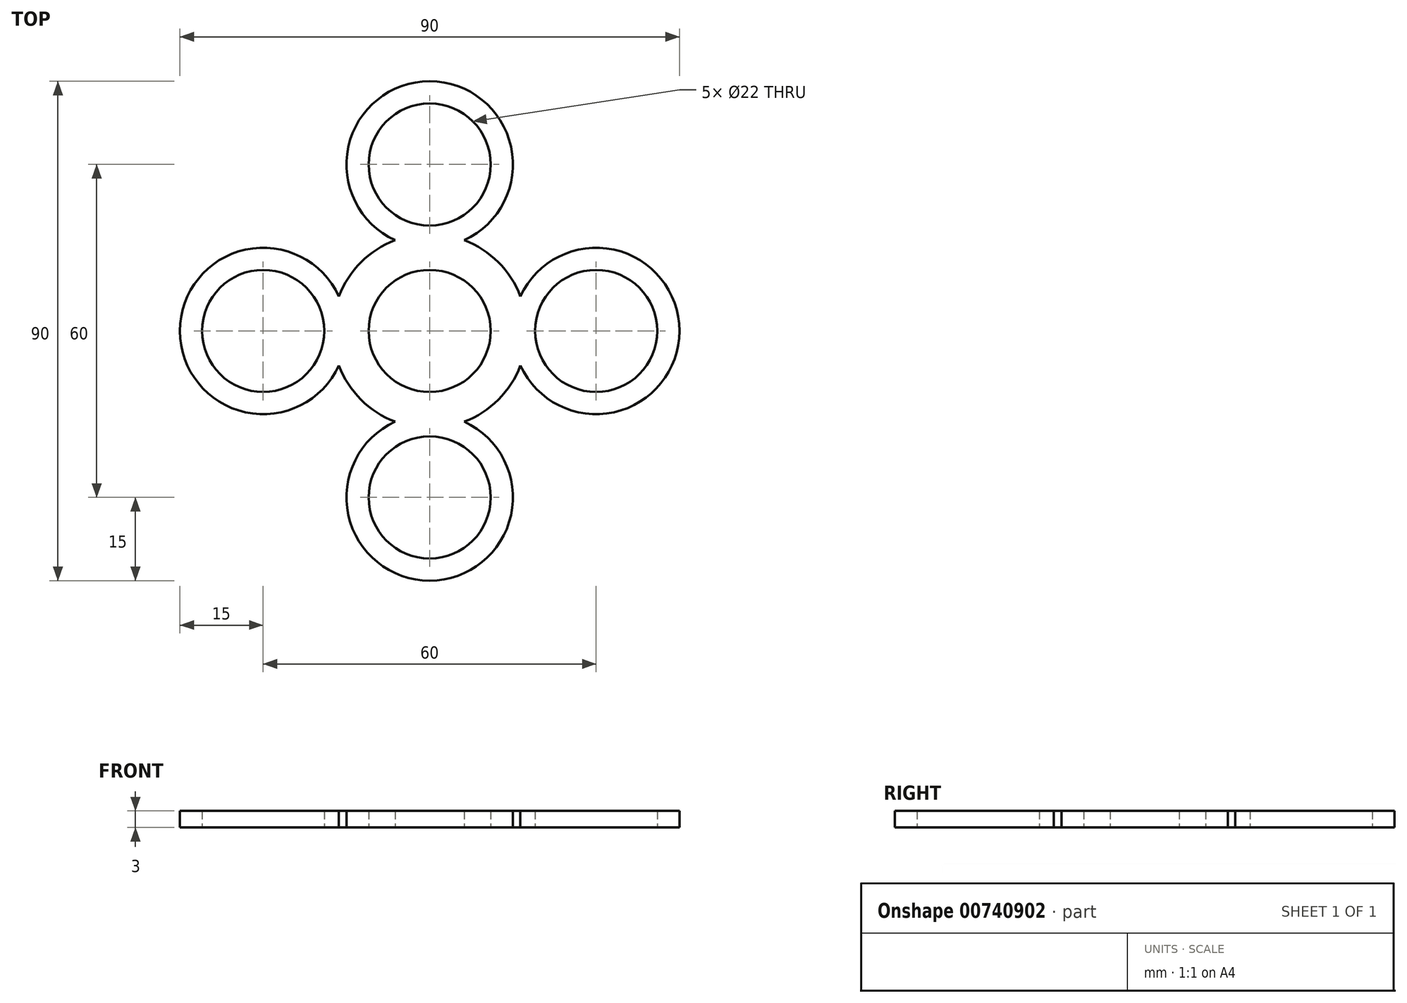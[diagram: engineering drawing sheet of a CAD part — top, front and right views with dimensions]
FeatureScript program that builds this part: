
annotation { "Feature Type Name" : "Feature", "Feature Type Description" : "" }
export const myFeature = defineFeature(function(context is Context, id is Id, definition is map)
    precondition{}
    {
        {
            var Q0;
            Q0=qCreatedBy(makeId("Top.planeOp"),FACE);
            var sketch = newSketch(context, id + "F0", { "sketchPlane" : qUnion([Q0])});
            skArc(sketch, "E0", {"start": v(7.78, 7.78) * mm, "mid": v(0, 11) * mm, "end": v(-7.78, 7.78) * mm});
            skArc(sketch, "E1", {"start": v(-6.23, 16.35) * mm, "mid": v(-9.51, 14.69) * mm, "end": v(-12.37, 12.37) * mm});
            skCircle(sketch, "E2", {"center": v(0, 30) * mm, "radius": 11 * mm});
            skArc(sketch, "E3", {"start": v(6.23, 16.35) * mm, "mid": v(0, 45) * mm, "end": v(-6.23, 16.35) * mm});
            skArc(sketch, "E4.trimOffspring", {"start": v(12.37, 12.37) * mm, "mid": v(9.51, 14.69) * mm, "end": v(6.23, 16.35) * mm});
            skArc(sketch, "E5.1.0", {"start": v(-16.35, 6.23) * mm, "mid": v(-45, 0) * mm, "end": v(-16.35, -6.23) * mm});
            skCircle(sketch, "E5.1.1", {"center": v(-30, 0) * mm, "radius": 11 * mm});
            skArc(sketch, "E5.1.2", {"start": v(-12.37, 12.37) * mm, "mid": v(-14.69, 9.51) * mm, "end": v(-16.35, 6.23) * mm});
            skArc(sketch, "E5.1.3", {"start": v(-16.35, -6.23) * mm, "mid": v(-14.69, -9.51) * mm, "end": v(-12.37, -12.37) * mm});
            skArc(sketch, "E5.1.4", {"start": v(-7.78, 7.78) * mm, "mid": v(-11, 0) * mm, "end": v(-7.78, -7.78) * mm});
            skArc(sketch, "E5.2.0", {"start": v(-6.23, -16.35) * mm, "mid": v(0, -45) * mm, "end": v(6.23, -16.35) * mm});
            skCircle(sketch, "E5.2.1", {"center": v(0, -30) * mm, "radius": 11 * mm});
            skArc(sketch, "E5.2.2", {"start": v(-12.37, -12.37) * mm, "mid": v(-9.51, -14.69) * mm, "end": v(-6.23, -16.35) * mm});
            skArc(sketch, "E5.2.3", {"start": v(6.23, -16.35) * mm, "mid": v(9.51, -14.69) * mm, "end": v(12.37, -12.37) * mm});
            skArc(sketch, "E5.2.4", {"start": v(-7.78, -7.78) * mm, "mid": v(0, -11) * mm, "end": v(7.78, -7.78) * mm});
            skArc(sketch, "E5.3.0", {"start": v(16.35, -6.23) * mm, "mid": v(45, 0) * mm, "end": v(16.35, 6.23) * mm});
            skCircle(sketch, "E5.3.1", {"center": v(30, 0) * mm, "radius": 11 * mm});
            skArc(sketch, "E5.3.2", {"start": v(12.37, -12.37) * mm, "mid": v(14.69, -9.51) * mm, "end": v(16.35, -6.23) * mm});
            skArc(sketch, "E5.3.3", {"start": v(16.35, 6.23) * mm, "mid": v(14.69, 9.51) * mm, "end": v(12.37, 12.37) * mm});
            skArc(sketch, "E5.3.4", {"start": v(7.78, -7.78) * mm, "mid": v(11, 0) * mm, "end": v(7.78, 7.78) * mm});
            skSolve(sketch);
        }
        {
            var Q0;
            Q0 = qSketchRegion(id + "F0", true);
            extrude(context, id + "F1", {"entities" : qUnion([Q0]), "depth" : 3 * mm, "offsetDistance" : 25 * mm});
        }
    });
